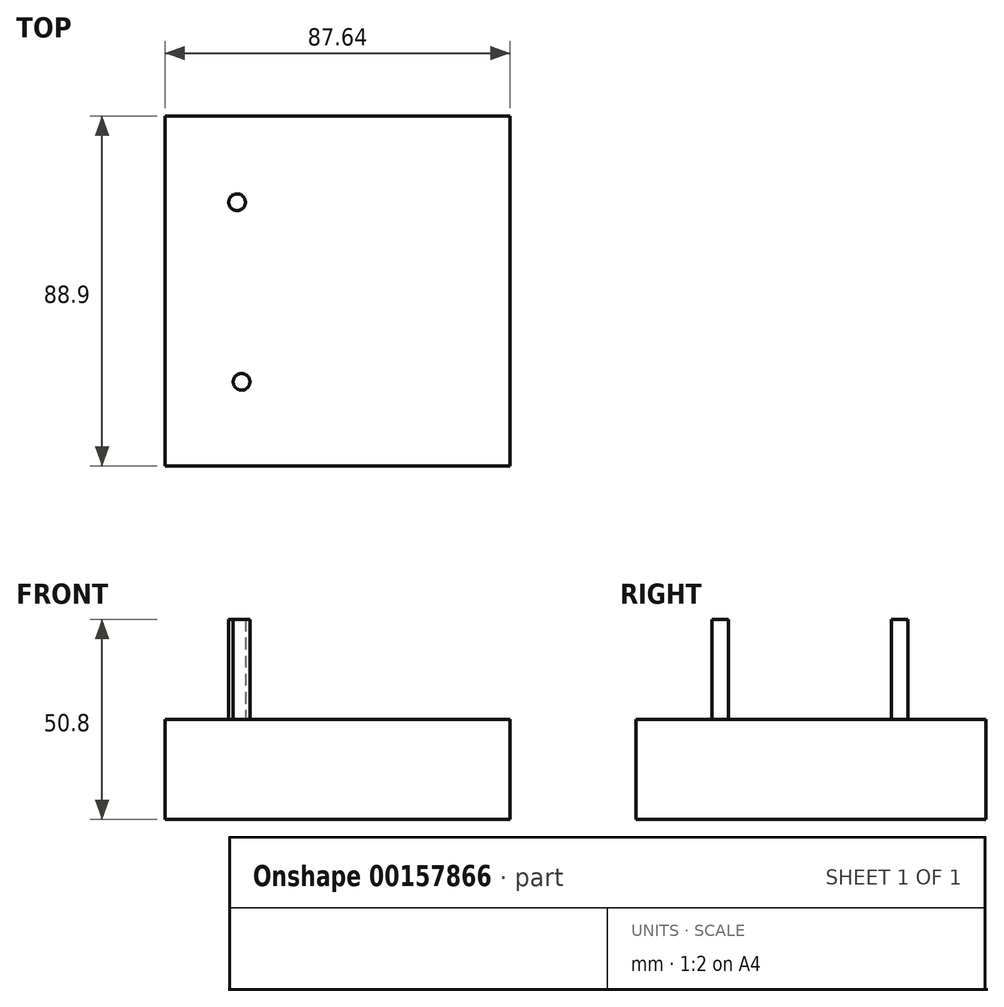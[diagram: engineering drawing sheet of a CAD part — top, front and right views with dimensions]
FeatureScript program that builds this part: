
annotation { "Feature Type Name" : "Feature", "Feature Type Description" : "" }
export const myFeature = defineFeature(function(context is Context, id is Id, definition is map)
    precondition{}
    {
        {
            var Q0;
            Q0=qCreatedBy(makeId("Top.planeOp"),FACE);
            var sketch = newSketch(context, id + "F0", { "sketchPlane" : qUnion([Q0])});
            skLineSegment(sketch, "E0.bottom", {"start": v(43.82, -44.45) * mm, "end": v(-43.82, -44.45) * mm});
            skLineSegment(sketch, "E0.top", {"start": v(43.82, 44.45) * mm, "end": v(-43.82, 44.45) * mm});
            skLineSegment(sketch, "E0.left", {"start": v(43.82, -44.45) * mm, "end": v(43.82, 44.45) * mm});
            skLineSegment(sketch, "E0.right", {"start": v(-43.82, -44.45) * mm, "end": v(-43.82, 44.45) * mm});
            skPoint(sketch, "E0.middle", {"position": v(0, 0) * mm});
            skSolve(sketch);
        }
        {
            var Q0;
            Q0=makeQuery(id+"F0.imprint","IMPRINT",FACE,{"disambiguationData":[TD([[makeQuery(id+"F0.imprint","IMPRINT",EDGE,{"derivedFrom":sQuery(id+"F0.wireOp",EDGE,"E0.bottom")}),-1.0]])]});
            extrude(context, id + "F1", {"entities" : qUnion([Q0]), "depth" : 25.4 * mm});
        }
        {
            var Q0;
            Q0=makeQuery(id+"F1.opExtrude","CAP_FACE",FACE,{"disambiguationData":[OSD([sQuery(id+"F0.wireOp",EDGE,"E0.bottom"),sQuery(id+"F0.wireOp",EDGE,"E0.top"),sQuery(id+"F0.wireOp",EDGE,"E0.left"),sQuery(id+"F0.wireOp",EDGE,"E0.right")])],"isStart":false});
            var sketch = newSketch(context, id + "F2", { "sketchPlane" : qUnion([Q0])});
            skCircle(sketch, "E1", {"center": v(-25.52, 22.56) * mm, "radius": 2.12 * mm});
            skCircle(sketch, "E2", {"center": v(-24.38, -23.07) * mm, "radius": 2.12 * mm});
            skLineSegment(sketch, "E3", {"start": v(-23.94, 44.45) * mm, "end": v(-21.73, -44.45) * mm});
            skSolve(sketch);
        }
        {
            var Q0;
            Q0=makeQuery(id+"F2.imprint","IMPRINT",FACE,{"disambiguationData":[TD([[makeQuery(id+"F2.imprint","IMPRINT",EDGE,{"derivedFrom":sQuery(id+"F2.wireOp",EDGE,"E1")}),1.0]])]});
            extrude(context, id + "F3", {"entities" : qUnion([Q0]), "operationType" : NewBodyOperationType.ADD, "depth" : 25.4 * mm, "offsetDistance" : 25.4 * mm});
        }
        {
            var Q0;
            Q0=makeQuery(id+"F2.imprint","IMPRINT",FACE,{"disambiguationData":[TD([[makeQuery(id+"F2.imprint","IMPRINT",EDGE,{"derivedFrom":sQuery(id+"F2.wireOp",EDGE,"E2")}),1.0]])]});
            var Q1;
            Q1=sQuery(id+"F2.wireOp",EDGE,"E2");
            extrude(context, id + "F4", {"entities" : qUnion([Q0]), "operationType" : NewBodyOperationType.ADD, "surfaceEntities" : qUnion([Q1]), "depth" : 25.4 * mm, "offsetDistance" : 25.4 * mm});
        }
    });
